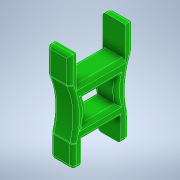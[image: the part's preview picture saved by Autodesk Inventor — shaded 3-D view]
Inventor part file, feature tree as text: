
AUTODESK INVENTOR PART (.ipt)
format: ipt  version: 2022 (Build 260153000, 153)  size: 221,696 bytes
history: native  units: in
note: dims shown in document units (in); Inventor stores cm internally (conversion verified against a paired STEP export)
features: extrude x1, fillet x1, sketch x1
ambient origin geometry x8: Origin, YZ Plane, XZ Plane, XY Plane, X Axis, Y Axis, Z Axis, Center Point
bodies: Body1 (feature_tree)
feature tree (3):
  extrude  "Extrusion2"  Depth=0.125in
  fillet  "Fillet2"  [1 undecoded]
  sketch  "Sketch2"  dims[d3=0.8661in d4=0.0in d5=0.125in]
note: 1 required parameter value undecoded (feature->parameter linkage not recoverable at this tier; creation-order binding heuristic only, values carry confidence <= 0.55)
